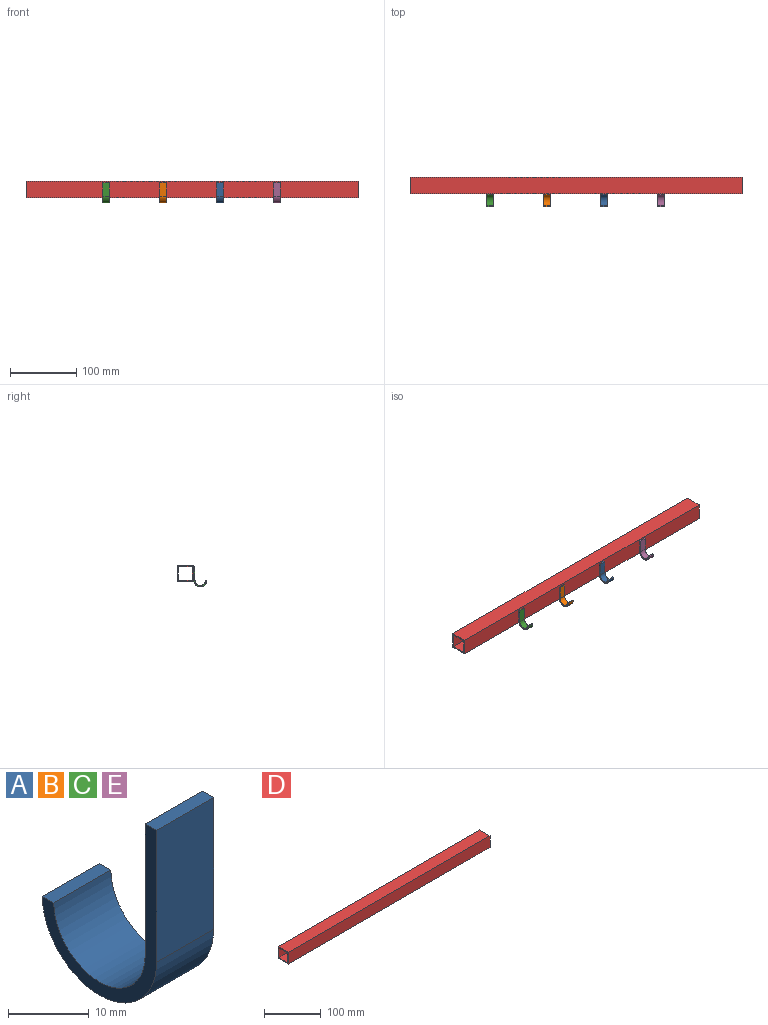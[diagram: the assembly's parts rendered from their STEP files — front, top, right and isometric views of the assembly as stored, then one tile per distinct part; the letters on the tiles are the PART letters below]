
ASSEMBLY  parts=5 mates=4
PART A: 8 faces, bbox 10x20x30 mm
  f0: plane 20x10mm, normal (0,-1,0), area 200mm2, adj f1,f5,f6,f7
  f1: cylinder r=10mm len=20mm, axis (-1,0,0), area 314.2mm2, adj f0,f2,f6,f7
  f2: plane 10x2mm, normal (0,0,1), area 20mm2, adj f1,f3,f6,f7
  f3: cylinder r=8mm len=16mm, axis (-1,0,0), area 251.3mm2, adj f2,f4,f6,f7
  f4: plane 20x10mm, normal (0,1,0), area 200mm2, adj f3,f5,f6,f7
  f5: plane 10x2mm, normal (0,0,1), area 20mm2, adj f0,f4,f6,f7
  f6: plane 30x20mm, normal (1,0,0), area 96.5mm2, adj f0,f1,f2,f3,f4,f5
  f7: plane 30x20mm, normal (-1,0,0), area 96.5mm2, adj f0,f1,f2,f3,f4,f5
PART B: same geometry as A
PART C: same geometry as A
PART D: 10 faces, bbox 501.3x25x25 mm
  f0: plane 501.26x21mm, normal (0,0,1), area 10526.4mm2, adj f1,f7,f8,f9
  f1: plane 501.26x21mm, normal (0,1,0), area 10526.4mm2, adj f0,f2,f8,f9
  f2: plane 501.26x21mm, normal (0,0,-1), area 10526.4mm2, adj f1,f7,f8,f9
  f3: plane 501.26x25mm, normal (0,-1,0), area 12531.5mm2, adj f4,f6,f8,f9
  f4: plane 501.26x25mm, normal (0,0,-1), area 12531.5mm2, adj f3,f5,f8,f9
  f5: plane 501.26x25mm, normal (0,1,0), area 12531.5mm2, adj f4,f6,f8,f9
  f6: plane 501.26x25mm, normal (0,0,1), area 12531.5mm2, adj f3,f5,f8,f9
  f7: plane 501.26x21mm, normal (0,-1,0), area 10526.4mm2, adj f0,f2,f8,f9
  f8: plane 25x25mm, normal (1,0,0), area 184mm2, adj f0,f1,f2,f3,f4,f5,f6,f7
  f9: plane 25x25mm, normal (-1,0,0), area 184mm2, adj f0,f1,f2,f3,f4,f5,f6,f7
PART E: same geometry as A
PLACE A rot(axis=(0,0,1),180deg) t=(62.68,73.88,-7.6)mm
PLACE B rot(axis=(0,0,1),180deg) t=(-23.32,73.88,-7.6)mm
PLACE C rot(axis=(0,0,1),180deg) t=(-109.32,73.88,-7.6)mm
PLACE D t=(-235.32,86.38,2.4)mm fixed
PLACE E rot(axis=(0,0,1),180deg) t=(148.68,73.88,-7.6)mm
MATE fastened D.f3 <-> C.f0  axis (0,-1,0) through (-235.32,73.88,2.4)mm
MATE fastened D.f3 <-> A.f0  axis (0,-1,0) through (-235.32,73.88,2.4)mm
MATE fastened D.f3 <-> E.f0  axis (0,-1,0) through (-235.32,73.88,2.4)mm
MATE fastened D.f3 <-> B.f0  axis (0,-1,0) through (-235.32,73.88,2.4)mm
